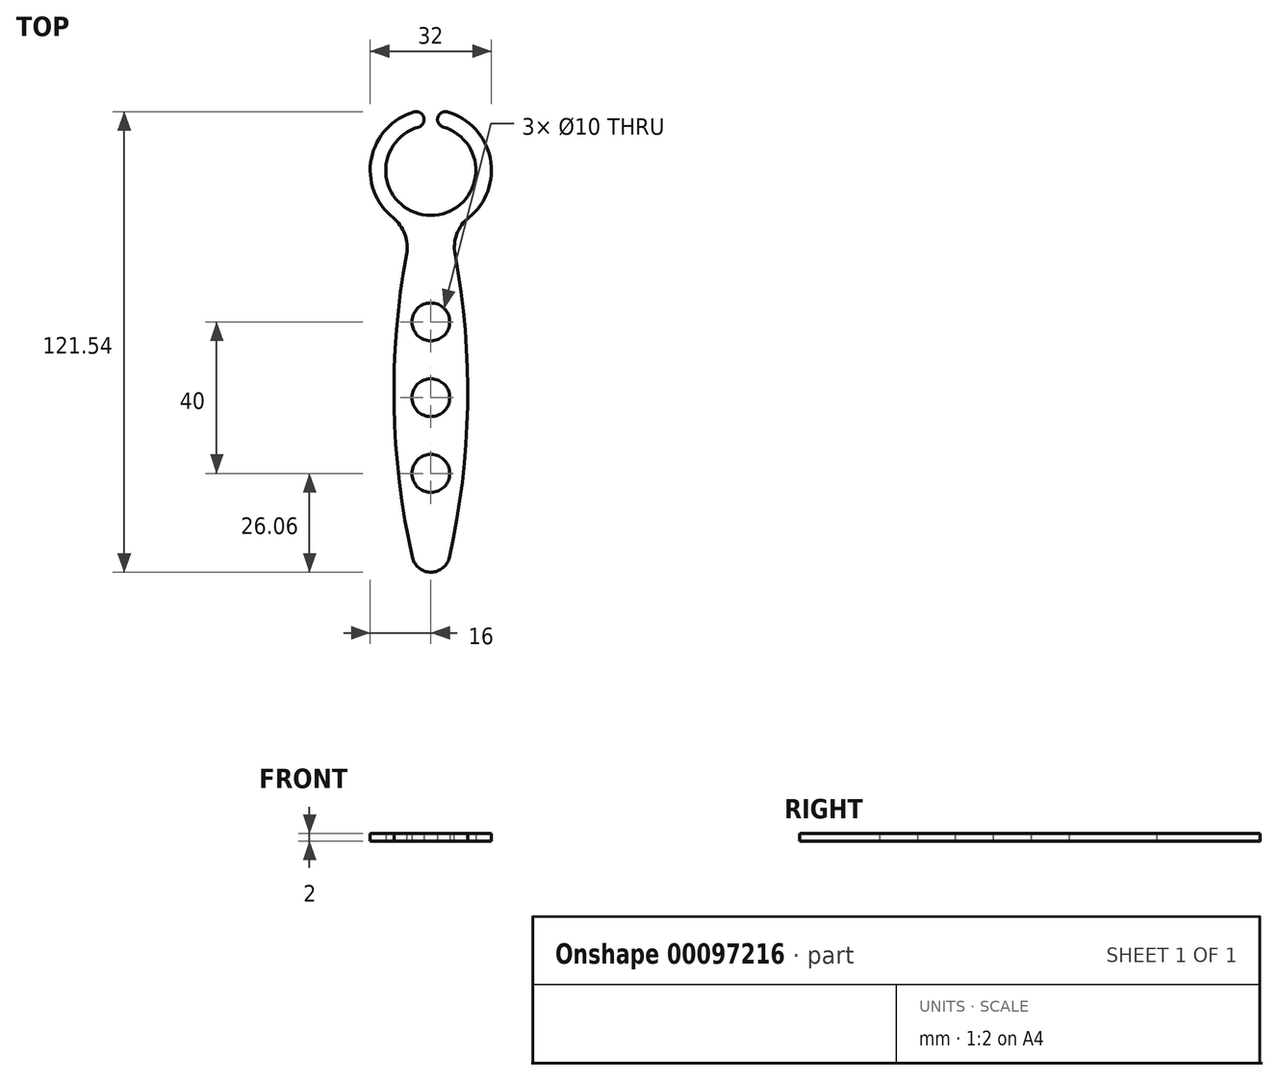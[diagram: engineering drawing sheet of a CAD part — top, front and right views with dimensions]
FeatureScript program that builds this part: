
annotation { "Feature Type Name" : "Feature", "Feature Type Description" : "" }
export const myFeature = defineFeature(function(context is Context, id is Id, definition is map)
    precondition{}
    {
        {
            var Q0;
            Q0=qCreatedBy(makeId("Top.planeOp"),FACE);
            var sketch = newSketch(context, id + "F0", { "sketchPlane" : qUnion([Q0])});
            skCircle(sketch, "E0", {"center": v(0, 0) * mm, "radius": 12 * mm, "construction": true});
            skArc(sketch, "E1", {"start": v(-1.55, 11.8) * mm, "mid": v(0, -11.9) * mm, "end": v(1.55, 11.8) * mm});
            skLineSegment(sketch, "E2", {"start": v(-1.55, 11.8) * mm, "end": v(0, 0) * mm, "construction": true});
            skLineSegment(sketch, "E3", {"start": v(1.55, 11.8) * mm, "end": v(0, 0) * mm, "construction": true});
            skArc(sketch, "E4", {"start": v(-2.09, 15.86) * mm, "mid": v(-15.93, 1.5) * mm, "end": v(-5, -15.2) * mm});
            skLineSegment(sketch, "E5", {"start": v(-1.55, 11.8) * mm, "end": v(-2.09, 15.86) * mm});
            skLineSegment(sketch, "E6", {"start": v(1.55, 11.8) * mm, "end": v(2.09, 15.86) * mm});
            skLineSegment(sketch, "E7", {"start": v(0, 0) * mm, "end": v(0, -120) * mm, "construction": true});
            skArc(sketch, "E8.trimOffspring", {"start": v(5, -15.2) * mm, "mid": v(15.93, 1.5) * mm, "end": v(2.09, 15.86) * mm});
            skArc(sketch, "E9", {"start": v(-5, -15.2) * mm, "mid": v(-9.5, -67.93) * mm, "end": v(0, -120) * mm});
            skArc(sketch, "E10", {"start": v(0, -120) * mm, "mid": v(9.5, -67.93) * mm, "end": v(5, -15.2) * mm});
            skCircle(sketch, "E11", {"center": v(0, -80) * mm, "radius": 5 * mm});
            skCircle(sketch, "E12", {"center": v(0, -60) * mm, "radius": 5 * mm});
            skCircle(sketch, "E13", {"center": v(0, -40) * mm, "radius": 5 * mm});
            skSolve(sketch);
        }
        {
            var Q0;
            Q0 = qSketchRegion(id + "F0", true);
            extrude(context, id + "F1", {"entities" : qUnion([Q0]), "depth" : 2 * mm});
        }
        {
            var Q0;
            Q0=makeQuery(id+"F1.opExtrude","SWEPT_EDGE",EDGE,{"disambiguationData":[OSD([sQuery(id+"F0.wireOp",EDGE,"E8.trimOffspring"),sQuery(id+"F0.wireOp",EDGE,"E10")])]});
            var Q1;
            Q1=makeQuery(id+"F1.opExtrude","SWEPT_EDGE",EDGE,{"disambiguationData":[OSD([sQuery(id+"F0.wireOp",EDGE,"E4"),sQuery(id+"F0.wireOp",EDGE,"E9")])]});
            fillet(context, id + "F2", {"entities" : qUnion([Q0, Q1]), "radius" : 10 * mm, "tangentPropagation" : true, "allowEdgeOverflow" : false});
        }
        {
            var Q0;
            Q0=makeQuery(id+"F1.opExtrude","SWEPT_EDGE",EDGE,{"disambiguationData":[OSD([sQuery(id+"F0.wireOp",EDGE,"E9"),sQuery(id+"F0.wireOp",EDGE,"E10")])]});
            fillet(context, id + "F3", {"entities" : qUnion([Q0]), "radius" : 5 * mm, "tangentPropagation" : true, "allowEdgeOverflow" : false});
        }
        {
            var Q0;
            Q0=makeQuery(id+"F1.opExtrude","SWEPT_EDGE",EDGE,{"disambiguationData":[OSD([sQuery(id+"F0.wireOp",EDGE,"E1"),sQuery(id+"F0.wireOp",EDGE,"E5")])]});
            var Q1;
            Q1=makeQuery(id+"F1.opExtrude","SWEPT_EDGE",EDGE,{"disambiguationData":[OSD([sQuery(id+"F0.wireOp",EDGE,"E1"),sQuery(id+"F0.wireOp",EDGE,"E6")])]});
            var Q2;
            Q2=makeQuery(id+"F1.opExtrude","SWEPT_EDGE",EDGE,{"disambiguationData":[OSD([sQuery(id+"F0.wireOp",EDGE,"E4"),sQuery(id+"F0.wireOp",EDGE,"E5")])]});
            var Q3;
            Q3=makeQuery(id+"F1.opExtrude","SWEPT_EDGE",EDGE,{"disambiguationData":[OSD([sQuery(id+"F0.wireOp",EDGE,"E6"),sQuery(id+"F0.wireOp",EDGE,"E8.trimOffspring")])]});
            fillet(context, id + "F4", {"entities" : qUnion([Q0, Q1, Q2, Q3]), "radius" : 2 * mm, "tangentPropagation" : true, "allowEdgeOverflow" : false});
        }
    });
